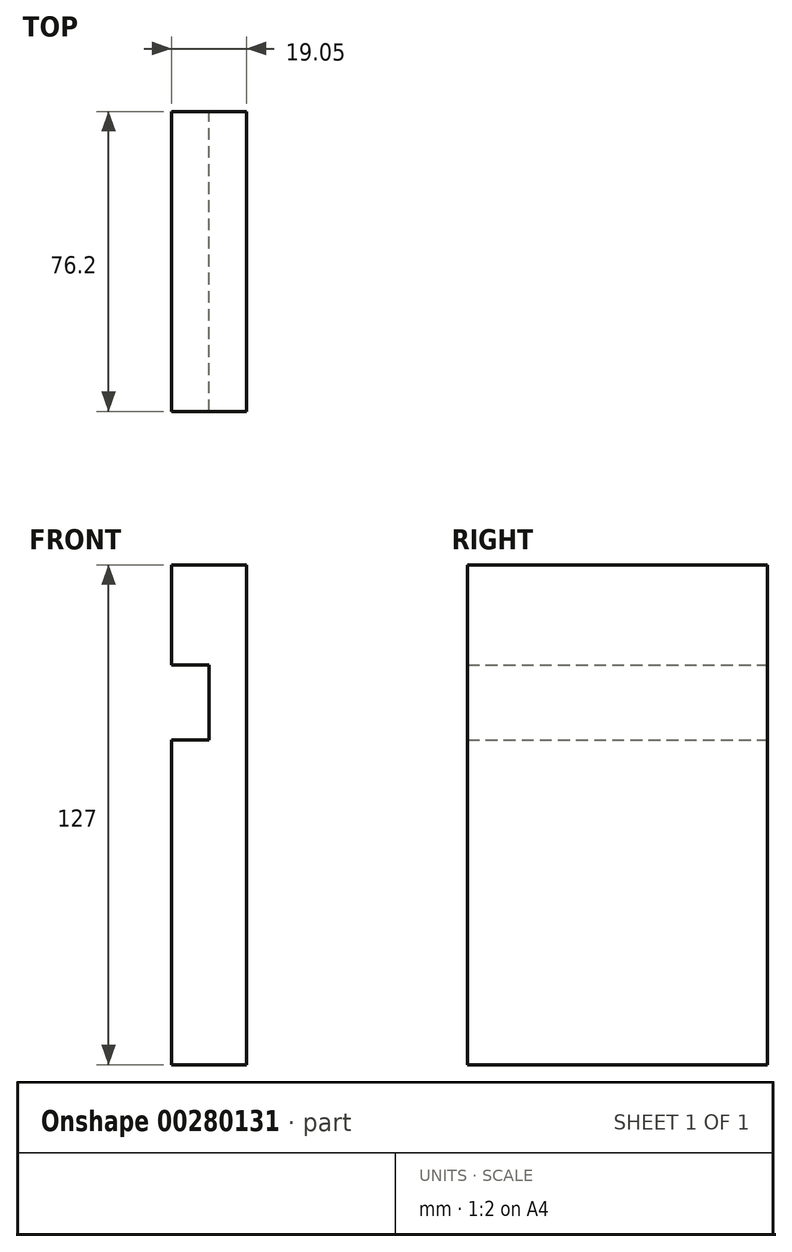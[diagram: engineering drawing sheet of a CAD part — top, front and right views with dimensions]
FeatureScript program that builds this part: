
annotation { "Feature Type Name" : "Feature", "Feature Type Description" : "" }
export const myFeature = defineFeature(function(context is Context, id is Id, definition is map)
    precondition{}
    {
        {
            var Q0;
            Q0=qCreatedBy(makeId("Front.planeOp"),FACE);
            var sketch = newSketch(context, id + "F0", { "sketchPlane" : qUnion([Q0])});
            skLineSegment(sketch, "E0", {"start": v(0, 0) * mm, "end": v(0, 127) * mm});
            skLineSegment(sketch, "E1", {"start": v(0, 127) * mm, "end": v(-19.05, 127) * mm});
            skLineSegment(sketch, "E2", {"start": v(-19.05, 127) * mm, "end": v(-19.05, 101.6) * mm});
            skLineSegment(sketch, "E3", {"start": v(-19.05, 101.6) * mm, "end": v(-9.52, 101.6) * mm});
            skLineSegment(sketch, "E4", {"start": v(-9.52, 101.6) * mm, "end": v(-9.52, 82.55) * mm});
            skLineSegment(sketch, "E5", {"start": v(-9.52, 82.55) * mm, "end": v(-19.05, 82.55) * mm});
            skLineSegment(sketch, "E6", {"start": v(-19.05, 82.55) * mm, "end": v(-19.05, 0) * mm});
            skLineSegment(sketch, "E7", {"start": v(0, 0) * mm, "end": v(-19.05, 0) * mm});
            skSolve(sketch);
        }
        {
            var Q0;
            Q0 = qSketchRegion(id + "F0", true);
            extrude(context, id + "F1", {"entities" : qUnion([Q0]), "depth" : 76.2 * mm});
        }
    });
